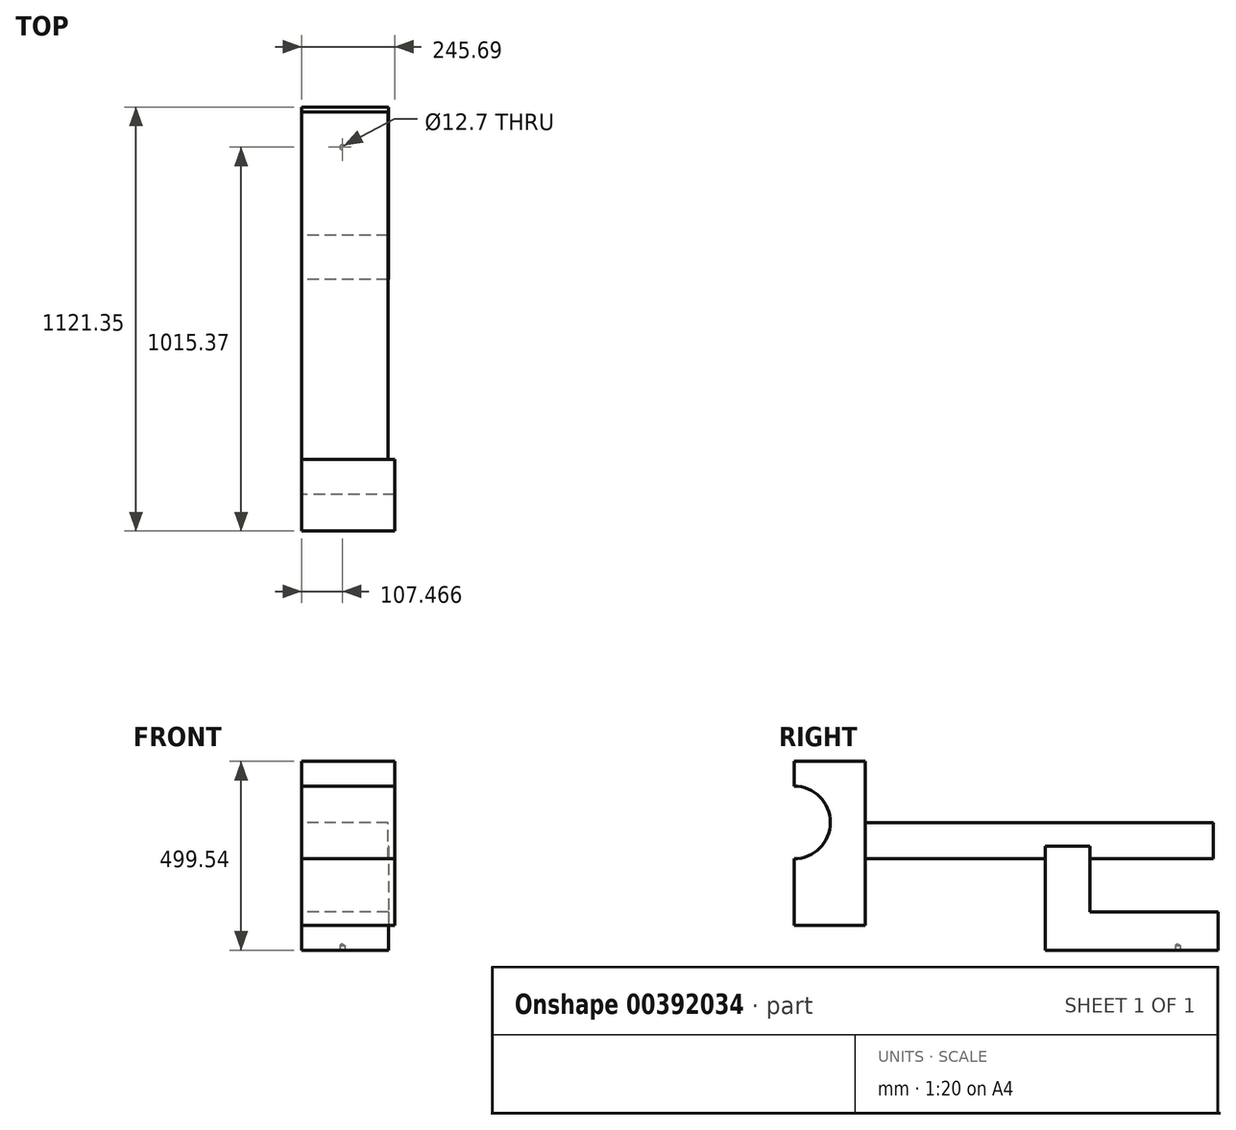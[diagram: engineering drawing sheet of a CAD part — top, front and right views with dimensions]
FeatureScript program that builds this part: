
annotation { "Feature Type Name" : "Feature", "Feature Type Description" : "" }
export const myFeature = defineFeature(function(context is Context, id is Id, definition is map)
    precondition{}
    {
        {
            var Q0;
            Q0=qCreatedBy(makeId("Right.planeOp"),FACE);
            var sketch = newSketch(context, id + "F0", { "sketchPlane" : qUnion([Q0])});
            skLineSegment(sketch, "E0.bottom", {"start": v(-670.54, 63.26) * mm, "end": v(444.1, 63.26) * mm});
            skLineSegment(sketch, "E0.top", {"start": v(-670.54, -32.86) * mm, "end": v(444.1, -32.86) * mm});
            skLineSegment(sketch, "E0.left", {"start": v(-670.54, 63.26) * mm, "end": v(-670.54, -32.86) * mm});
            skLineSegment(sketch, "E0.right", {"start": v(444.1, 63.26) * mm, "end": v(444.1, -32.86) * mm});
            skSolve(sketch);
        }
        {
            var Q0;
            Q0 = qSketchRegion(id + "F0", true);
            extrude(context, id + "F1", {"entities" : qUnion([Q0]), "depth" : 228.6 * mm});
        }
        {
            var Q0;
            Q0=qCreatedBy(makeId("Right.planeOp"),FACE);
            var sketch = newSketch(context, id + "F2", { "sketchPlane" : qUnion([Q0])});
            skLineSegment(sketch, "E1.bottom", {"start": v(0, 0) * mm, "end": v(117.2, 0) * mm});
            skLineSegment(sketch, "E1.top", {"start": v(0, -274.6) * mm, "end": v(117.2, -274.6) * mm});
            skLineSegment(sketch, "E1.left", {"start": v(0, 0) * mm, "end": v(0, -274.6) * mm});
            skLineSegment(sketch, "E1.right", {"start": v(117.2, 0) * mm, "end": v(117.2, -274.6) * mm});
            skSolve(sketch);
        }
        {
            var Q0;
            Q0 = qSketchRegion(id + "F2", true);
            extrude(context, id + "F3", {"entities" : qUnion([Q0]), "operationType" : NewBodyOperationType.ADD, "depth" : 229.33 * mm});
        }
        {
            var Q0;
            Q0=makeQuery(id+"F3.opExtrude","SWEPT_FACE",FACE,{"disambiguationData":[OSD([sQuery(id+"F2.wireOp",EDGE,"E1.top")])]});
            var sketch = newSketch(context, id + "F4", { "sketchPlane" : qUnion([Q0])});
            skLineSegment(sketch, "E2.bottom", {"start": v(0, 0) * mm, "end": v(0, 0) * mm});
            skLineSegment(sketch, "E2.top", {"start": v(0, 0) * mm, "end": v(0, 0) * mm});
            skLineSegment(sketch, "E2.left", {"start": v(0, 0) * mm, "end": v(0, 0) * mm});
            skLineSegment(sketch, "E2.right", {"start": v(0, 0) * mm, "end": v(0, 0) * mm});
            skLineSegment(sketch, "E3.bottom", {"start": v(0, 0) * mm, "end": v(229.33, 0) * mm});
            skLineSegment(sketch, "E3.top", {"start": v(0, -456.35) * mm, "end": v(229.33, -456.35) * mm});
            skLineSegment(sketch, "E3.left", {"start": v(0, 0) * mm, "end": v(0, -456.35) * mm});
            skLineSegment(sketch, "E3.right", {"start": v(229.33, 0) * mm, "end": v(229.33, -456.35) * mm});
            skSolve(sketch);
        }
        {
            var Q0;
            Q0 = qSketchRegion(id + "F4", true);
            extrude(context, id + "F5", {"entities" : qUnion([Q0]), "operationType" : NewBodyOperationType.ADD, "oppositeDirection" : true, "depth" : 101.28 * mm});
        }
        {
            var Q0;
            Q0=qCreatedBy(makeId("Right.planeOp"),FACE);
            var sketch = newSketch(context, id + "F6", { "sketchPlane" : qUnion([Q0])});
            skLineSegment(sketch, "E4.bottom", {"start": v(-665, 224.94) * mm, "end": v(-475.94, 224.94) * mm});
            skLineSegment(sketch, "E4.top", {"start": v(-665, -208.95) * mm, "end": v(-475.94, -208.95) * mm});
            skLineSegment(sketch, "E4.left", {"start": v(-665, 224.94) * mm, "end": v(-665, -208.95) * mm});
            skLineSegment(sketch, "E4.right", {"start": v(-475.94, 224.94) * mm, "end": v(-475.94, -208.95) * mm});
            skSolve(sketch);
        }
        {
            var Q0;
            Q0=makeQuery(id+"F6.imprint","IMPRINT",FACE,{"disambiguationData":[TD([[makeQuery(id+"F6.imprint","IMPRINT",EDGE,{"derivedFrom":sQuery(id+"F6.wireOp",EDGE,"E4.bottom")}),-1.0]])]});
            extrude(context, id + "F7", {"entities" : qUnion([Q0]), "operationType" : NewBodyOperationType.ADD, "depth" : 245.7 * mm});
        }
        {
            var Q0;
            Q0=makeQuery(id+"F7.boolean.opBoolean","MERGE",FACE,{"derivedFrom":[makeQuery(id+"F5.boolean.opBoolean","MERGE",FACE,{"derivedFrom":[makeQuery(id+"F3.boolean.opBoolean","MERGE",FACE,{"derivedFrom":[makeQuery(id+"F1.opExtrude","CAP_FACE",FACE,{"disambiguationData":[OSD([sQuery(id+"F0.wireOp",EDGE,"E0.bottom"),sQuery(id+"F0.wireOp",EDGE,"E0.top"),sQuery(id+"F0.wireOp",EDGE,"E0.left"),sQuery(id+"F0.wireOp",EDGE,"E0.right")])],"isStart":true}),makeQuery(id+"F3.opExtrude","CAP_FACE",FACE,{"disambiguationData":[OSD([sQuery(id+"F2.wireOp",EDGE,"E1.bottom"),sQuery(id+"F2.wireOp",EDGE,"E1.top"),sQuery(id+"F2.wireOp",EDGE,"E1.left"),sQuery(id+"F2.wireOp",EDGE,"E1.right")])],"isStart":true})]}),makeQuery(id+"F5.opExtrude","SWEPT_FACE",FACE,{"disambiguationData":[OSD([sQuery(id+"F4.wireOp",EDGE,"E3.left")])]})]}),makeQuery(id+"F7.opExtrude","CAP_FACE",FACE,{"disambiguationData":[OSD([sQuery(id+"F6.wireOp",EDGE,"E4.bottom"),sQuery(id+"F6.wireOp",EDGE,"E4.top"),sQuery(id+"F6.wireOp",EDGE,"E4.left"),sQuery(id+"F6.wireOp",EDGE,"E4.right")])],"isStart":true})]});
            var sketch = newSketch(context, id + "F8", { "sketchPlane" : qUnion([Q0])});
            skCircle(sketch, "E5", {"center": v(665, 63.26) * mm, "radius": 96.27 * mm});
            skSolve(sketch);
        }
        {
            var Q0;
            Q0 = qSketchRegion(id + "F8", true);
            extrude(context, id + "F9", {"entities" : qUnion([Q0]), "operationType" : NewBodyOperationType.REMOVE, "oppositeDirection" : true, "depth" : 484.47 * mm});
        }
        {
            var Q0;
            Q0=makeQuery(id+"F5.boolean.opBoolean","MERGE",FACE,{"derivedFrom":[makeQuery(id+"F3.opExtrude","SWEPT_FACE",FACE,{"disambiguationData":[OSD([sQuery(id+"F2.wireOp",EDGE,"E1.top")])]}),makeQuery(id+"F5.opExtrude","CAP_FACE",FACE,{"disambiguationData":[OSD([sQuery(id+"F4.wireOp",EDGE,"E3.bottom"),sQuery(id+"F4.wireOp",EDGE,"E3.top"),sQuery(id+"F4.wireOp",EDGE,"E3.left"),sQuery(id+"F4.wireOp",EDGE,"E3.right")])],"isStart":true})]});
            var sketch = newSketch(context, id + "F10", { "sketchPlane" : qUnion([Q0])});
            skPoint(sketch, "E6", {"position": v(107.47, -350.37) * mm});
            skSolve(sketch);
        }
        {
            var Q0;
            Q0=sQuery(id+"F10.wireOp",VERTEX,"E6");
            var Q1;
            Q1=makeQuery(id+"F1.opExtrude","SWEPT_BODY",BODY,{"disambiguationData":[OSD([sQuery(id+"F0.wireOp",EDGE,"E0.bottom"),sQuery(id+"F0.wireOp",EDGE,"E0.top"),sQuery(id+"F0.wireOp",EDGE,"E0.left"),sQuery(id+"F0.wireOp",EDGE,"E0.right")])]});
            hole(context, id + "F11", {"style" : HoleStyle.SIMPLE, "endStyle" : HoleEndStyle.BLIND, "holeDiameter" : 12.7 * mm, "holeDepth" : 12.7 * mm, "isTappedThrough" : true, "tappedDepth" : 12.7 * mm, "tapClearance" : 3, "locations" : qUnion([Q0]), "scope" : qUnion([Q1])});
        }
    });
